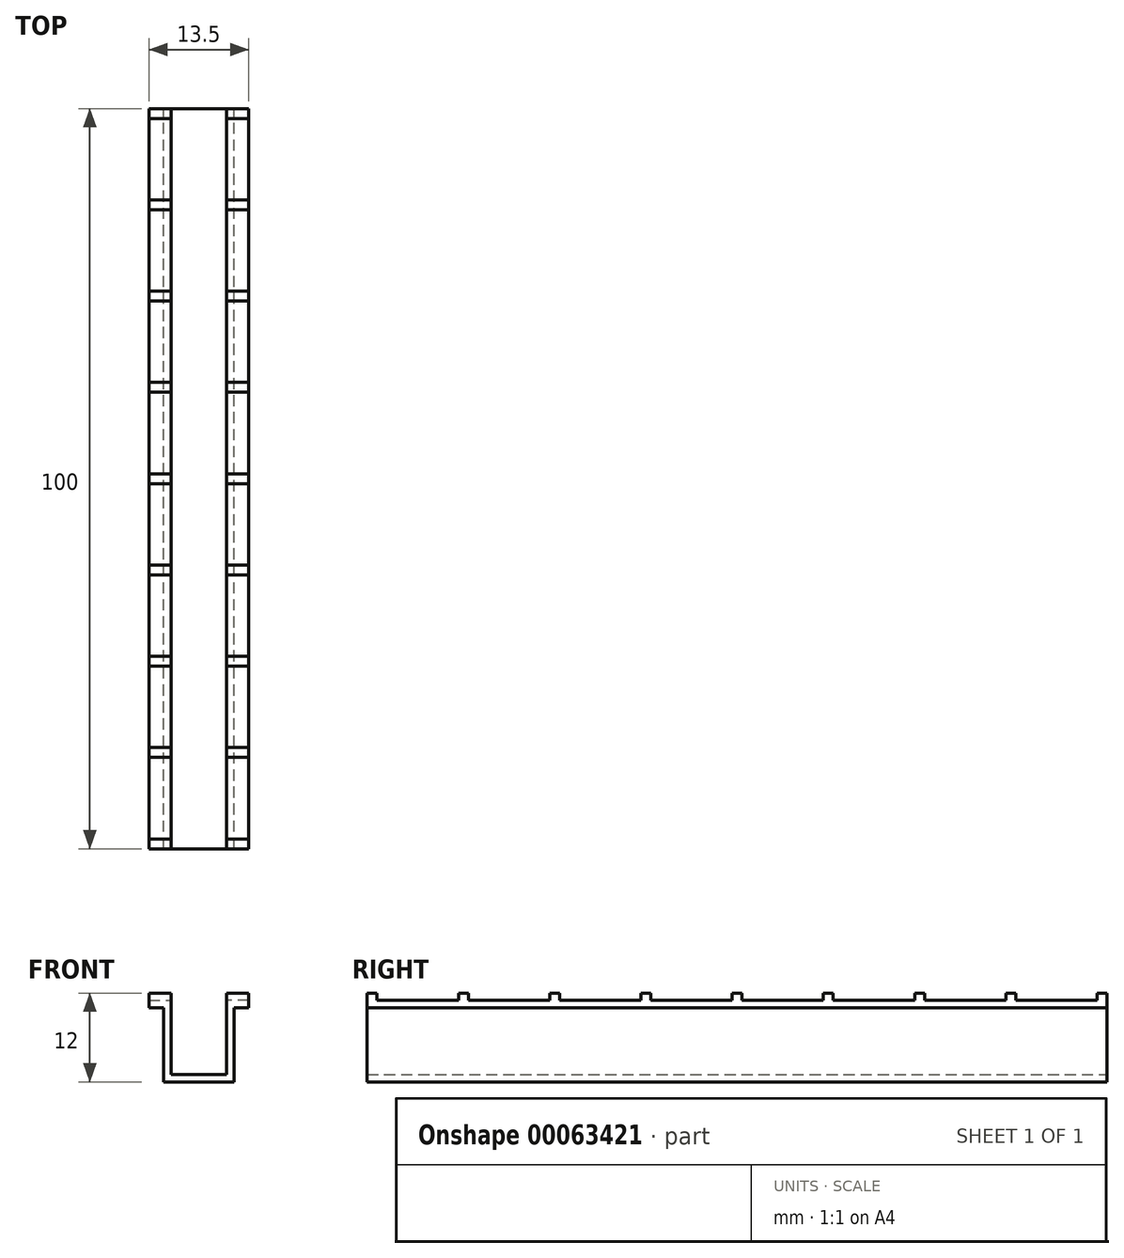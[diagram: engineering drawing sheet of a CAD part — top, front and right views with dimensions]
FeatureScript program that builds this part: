
annotation { "Feature Type Name" : "Feature", "Feature Type Description" : "" }
export const myFeature = defineFeature(function(context is Context, id is Id, definition is map)
    precondition{}
    {
        {
            var Q0;
            Q0=qCreatedBy(makeId("Front.planeOp"),FACE);
            var sketch = newSketch(context, id + "F0", { "sketchPlane" : qUnion([Q0])});
            skLineSegment(sketch, "E0", {"start": v(0, 0) * mm, "end": v(3, 0) * mm});
            skLineSegment(sketch, "E1", {"start": v(3, 0) * mm, "end": v(3, -10) * mm});
            skLineSegment(sketch, "E2", {"start": v(3, -10) * mm, "end": v(10.5, -10) * mm});
            skLineSegment(sketch, "E3", {"start": v(10.5, -10) * mm, "end": v(10.5, 0) * mm});
            skLineSegment(sketch, "E4.1.0.1", {"start": v(10.5, 0) * mm, "end": v(13.5, 0) * mm});
            skLineSegment(sketch, "E5.0", {"start": v(11.5, -1) * mm, "end": v(13.5, -1) * mm});
            skLineSegment(sketch, "E5.1", {"start": v(0, -1) * mm, "end": v(2, -1) * mm});
            skLineSegment(sketch, "E5.2", {"start": v(2, -1) * mm, "end": v(2, -11) * mm});
            skLineSegment(sketch, "E5.3", {"start": v(2, -11) * mm, "end": v(11.5, -11) * mm});
            skLineSegment(sketch, "E5.4", {"start": v(11.5, -11) * mm, "end": v(11.5, -1) * mm});
            skLineSegment(sketch, "E6", {"start": v(0, 0) * mm, "end": v(0, -1) * mm});
            skLineSegment(sketch, "E7", {"start": v(13.5, 0) * mm, "end": v(13.5, -1) * mm});
            skSolve(sketch);
        }
        {
            var Q0;
            Q0 = qSketchRegion(id + "F0", true);
            extrude(context, id + "F1", {"entities" : qUnion([Q0]), "depth" : 100 * mm});
        }
        {
            var Q0;
            Q0=makeQuery(id+"F1.opExtrude","SWEPT_FACE",FACE,{"disambiguationData":[OSD([sQuery(id+"F0.wireOp",EDGE,"E0")])]});
            var sketch = newSketch(context, id + "F2", { "sketchPlane" : qUnion([Q0])});
            skLineSegment(sketch, "E8.bottom", {"start": v(0, 0) * mm, "end": v(3, 0) * mm});
            skLineSegment(sketch, "E8.top", {"start": v(0, -1.33) * mm, "end": v(3, -1.33) * mm});
            skLineSegment(sketch, "E8.left", {"start": v(0, 0) * mm, "end": v(0, -1.33) * mm});
            skLineSegment(sketch, "E8.right", {"start": v(3, 0) * mm, "end": v(3, -1.33) * mm});
            skLineSegment(sketch, "E9", {"start": v(6.75, -100) * mm, "end": v(6.75, -62.61) * mm, "construction": true});
            skPoint(sketch, "E10", {"position": v(6.75, -100) * mm});
            skLineSegment(sketch, "E11.MirrorCS", {"start": v(13.5, 0) * mm, "end": v(10.5, 0) * mm});
            skLineSegment(sketch, "E12.MirrorCS", {"start": v(13.5, -1.33) * mm, "end": v(10.5, -1.33) * mm});
            skLineSegment(sketch, "E13.MirrorCS", {"start": v(13.5, 0) * mm, "end": v(13.5, -1.33) * mm});
            skLineSegment(sketch, "E14.MirrorCS", {"start": v(10.5, 0) * mm, "end": v(10.5, -1.33) * mm});
            skLineSegment(sketch, "E15.0.1.0", {"start": v(0, -12.33) * mm, "end": v(3, -12.33) * mm});
            skLineSegment(sketch, "E15.0.1.1", {"start": v(13.5, -12.33) * mm, "end": v(10.5, -12.33) * mm});
            skLineSegment(sketch, "E15.0.1.2", {"start": v(13.5, -13.67) * mm, "end": v(10.5, -13.67) * mm});
            skLineSegment(sketch, "E15.0.1.3", {"start": v(0, -13.67) * mm, "end": v(3, -13.67) * mm});
            skLineSegment(sketch, "E15.0.1.4", {"start": v(3, -12.33) * mm, "end": v(3, -13.67) * mm});
            skLineSegment(sketch, "E15.0.1.5", {"start": v(10.5, -12.33) * mm, "end": v(10.5, -13.67) * mm});
            skLineSegment(sketch, "E15.0.1.6", {"start": v(13.5, -12.33) * mm, "end": v(13.5, -13.67) * mm});
            skLineSegment(sketch, "E15.0.1.7", {"start": v(0, -12.33) * mm, "end": v(0, -13.67) * mm});
            skLineSegment(sketch, "E15.0.2.0", {"start": v(0, -24.67) * mm, "end": v(3, -24.67) * mm});
            skLineSegment(sketch, "E15.0.2.1", {"start": v(13.5, -24.67) * mm, "end": v(10.5, -24.67) * mm});
            skLineSegment(sketch, "E15.0.2.2", {"start": v(13.5, -26) * mm, "end": v(10.5, -26) * mm});
            skLineSegment(sketch, "E15.0.2.3", {"start": v(0, -26) * mm, "end": v(3, -26) * mm});
            skLineSegment(sketch, "E15.0.2.4", {"start": v(3, -24.67) * mm, "end": v(3, -26) * mm});
            skLineSegment(sketch, "E15.0.2.5", {"start": v(10.5, -24.67) * mm, "end": v(10.5, -26) * mm});
            skLineSegment(sketch, "E15.0.2.6", {"start": v(13.5, -24.67) * mm, "end": v(13.5, -26) * mm});
            skLineSegment(sketch, "E15.0.2.7", {"start": v(0, -24.67) * mm, "end": v(0, -26) * mm});
            skLineSegment(sketch, "E15.0.3.0", {"start": v(0, -37) * mm, "end": v(3, -37) * mm});
            skLineSegment(sketch, "E15.0.3.1", {"start": v(13.5, -37) * mm, "end": v(10.5, -37) * mm});
            skLineSegment(sketch, "E15.0.3.2", {"start": v(13.5, -38.33) * mm, "end": v(10.5, -38.33) * mm});
            skLineSegment(sketch, "E15.0.3.3", {"start": v(0, -38.33) * mm, "end": v(3, -38.33) * mm});
            skLineSegment(sketch, "E15.0.3.4", {"start": v(3, -37) * mm, "end": v(3, -38.33) * mm});
            skLineSegment(sketch, "E15.0.3.5", {"start": v(10.5, -37) * mm, "end": v(10.5, -38.33) * mm});
            skLineSegment(sketch, "E15.0.3.6", {"start": v(13.5, -37) * mm, "end": v(13.5, -38.33) * mm});
            skLineSegment(sketch, "E15.0.3.7", {"start": v(0, -37) * mm, "end": v(0, -38.33) * mm});
            skLineSegment(sketch, "E15.0.4.0", {"start": v(0, -49.33) * mm, "end": v(3, -49.33) * mm});
            skLineSegment(sketch, "E15.0.4.1", {"start": v(13.5, -49.33) * mm, "end": v(10.5, -49.33) * mm});
            skLineSegment(sketch, "E15.0.4.2", {"start": v(13.5, -50.67) * mm, "end": v(10.5, -50.67) * mm});
            skLineSegment(sketch, "E15.0.4.3", {"start": v(0, -50.67) * mm, "end": v(3, -50.67) * mm});
            skLineSegment(sketch, "E15.0.4.4", {"start": v(3, -49.33) * mm, "end": v(3, -50.67) * mm});
            skLineSegment(sketch, "E15.0.4.5", {"start": v(10.5, -49.33) * mm, "end": v(10.5, -50.67) * mm});
            skLineSegment(sketch, "E15.0.4.6", {"start": v(13.5, -49.33) * mm, "end": v(13.5, -50.67) * mm});
            skLineSegment(sketch, "E15.0.4.7", {"start": v(0, -49.33) * mm, "end": v(0, -50.67) * mm});
            skLineSegment(sketch, "E15.0.5.0", {"start": v(0, -61.67) * mm, "end": v(3, -61.67) * mm});
            skLineSegment(sketch, "E15.0.5.1", {"start": v(13.5, -61.67) * mm, "end": v(10.5, -61.67) * mm});
            skLineSegment(sketch, "E15.0.5.2", {"start": v(13.5, -63) * mm, "end": v(10.5, -63) * mm});
            skLineSegment(sketch, "E15.0.5.3", {"start": v(0, -63) * mm, "end": v(3, -63) * mm});
            skLineSegment(sketch, "E15.0.5.4", {"start": v(3, -61.67) * mm, "end": v(3, -63) * mm});
            skLineSegment(sketch, "E15.0.5.5", {"start": v(10.5, -61.67) * mm, "end": v(10.5, -63) * mm});
            skLineSegment(sketch, "E15.0.5.6", {"start": v(13.5, -61.67) * mm, "end": v(13.5, -63) * mm});
            skLineSegment(sketch, "E15.0.5.7", {"start": v(0, -61.67) * mm, "end": v(0, -63) * mm});
            skLineSegment(sketch, "E15.0.6.0", {"start": v(0, -74) * mm, "end": v(3, -74) * mm});
            skLineSegment(sketch, "E15.0.6.1", {"start": v(13.5, -74) * mm, "end": v(10.5, -74) * mm});
            skLineSegment(sketch, "E15.0.6.2", {"start": v(13.5, -75.33) * mm, "end": v(10.5, -75.33) * mm});
            skLineSegment(sketch, "E15.0.6.3", {"start": v(0, -75.33) * mm, "end": v(3, -75.33) * mm});
            skLineSegment(sketch, "E15.0.6.4", {"start": v(3, -74) * mm, "end": v(3, -75.33) * mm});
            skLineSegment(sketch, "E15.0.6.5", {"start": v(10.5, -74) * mm, "end": v(10.5, -75.33) * mm});
            skLineSegment(sketch, "E15.0.6.6", {"start": v(13.5, -74) * mm, "end": v(13.5, -75.33) * mm});
            skLineSegment(sketch, "E15.0.6.7", {"start": v(0, -74) * mm, "end": v(0, -75.33) * mm});
            skLineSegment(sketch, "E15.0.7.0", {"start": v(0, -86.33) * mm, "end": v(3, -86.33) * mm});
            skLineSegment(sketch, "E15.0.7.1", {"start": v(13.5, -86.33) * mm, "end": v(10.5, -86.33) * mm});
            skLineSegment(sketch, "E15.0.7.2", {"start": v(13.5, -87.67) * mm, "end": v(10.5, -87.67) * mm});
            skLineSegment(sketch, "E15.0.7.3", {"start": v(0, -87.67) * mm, "end": v(3, -87.67) * mm});
            skLineSegment(sketch, "E15.0.7.4", {"start": v(3, -86.33) * mm, "end": v(3, -87.67) * mm});
            skLineSegment(sketch, "E15.0.7.5", {"start": v(10.5, -86.33) * mm, "end": v(10.5, -87.67) * mm});
            skLineSegment(sketch, "E15.0.7.6", {"start": v(13.5, -86.33) * mm, "end": v(13.5, -87.67) * mm});
            skLineSegment(sketch, "E15.0.7.7", {"start": v(0, -86.33) * mm, "end": v(0, -87.67) * mm});
            skLineSegment(sketch, "E15.0.8.0", {"start": v(0, -98.67) * mm, "end": v(3, -98.67) * mm});
            skLineSegment(sketch, "E15.0.8.1", {"start": v(13.5, -98.67) * mm, "end": v(10.5, -98.67) * mm});
            skLineSegment(sketch, "E15.0.8.2", {"start": v(13.5, -100) * mm, "end": v(10.5, -100) * mm});
            skLineSegment(sketch, "E15.0.8.3", {"start": v(0, -100) * mm, "end": v(3, -100) * mm});
            skLineSegment(sketch, "E15.0.8.4", {"start": v(3, -98.67) * mm, "end": v(3, -100) * mm});
            skLineSegment(sketch, "E15.0.8.5", {"start": v(10.5, -98.67) * mm, "end": v(10.5, -100) * mm});
            skLineSegment(sketch, "E15.0.8.6", {"start": v(13.5, -98.67) * mm, "end": v(13.5, -100) * mm});
            skLineSegment(sketch, "E15.0.8.7", {"start": v(0, -98.67) * mm, "end": v(0, -100) * mm});
            skLineSegment(sketch, "E15.direction1", {"start": v(0, -1.33) * mm, "end": v(25, -1.33) * mm, "construction": true});
            skLineSegment(sketch, "E15.direction2", {"start": v(0, -1.33) * mm, "end": v(0, -13.67) * mm, "construction": true});
            skSolve(sketch);
        }
        {
            var Q0;
            Q0 = qSketchRegion(id + "F2", true);
            extrude(context, id + "F3", {"entities" : qUnion([Q0]), "operationType" : NewBodyOperationType.ADD, "depth" : 1 * mm});
        }
    });
